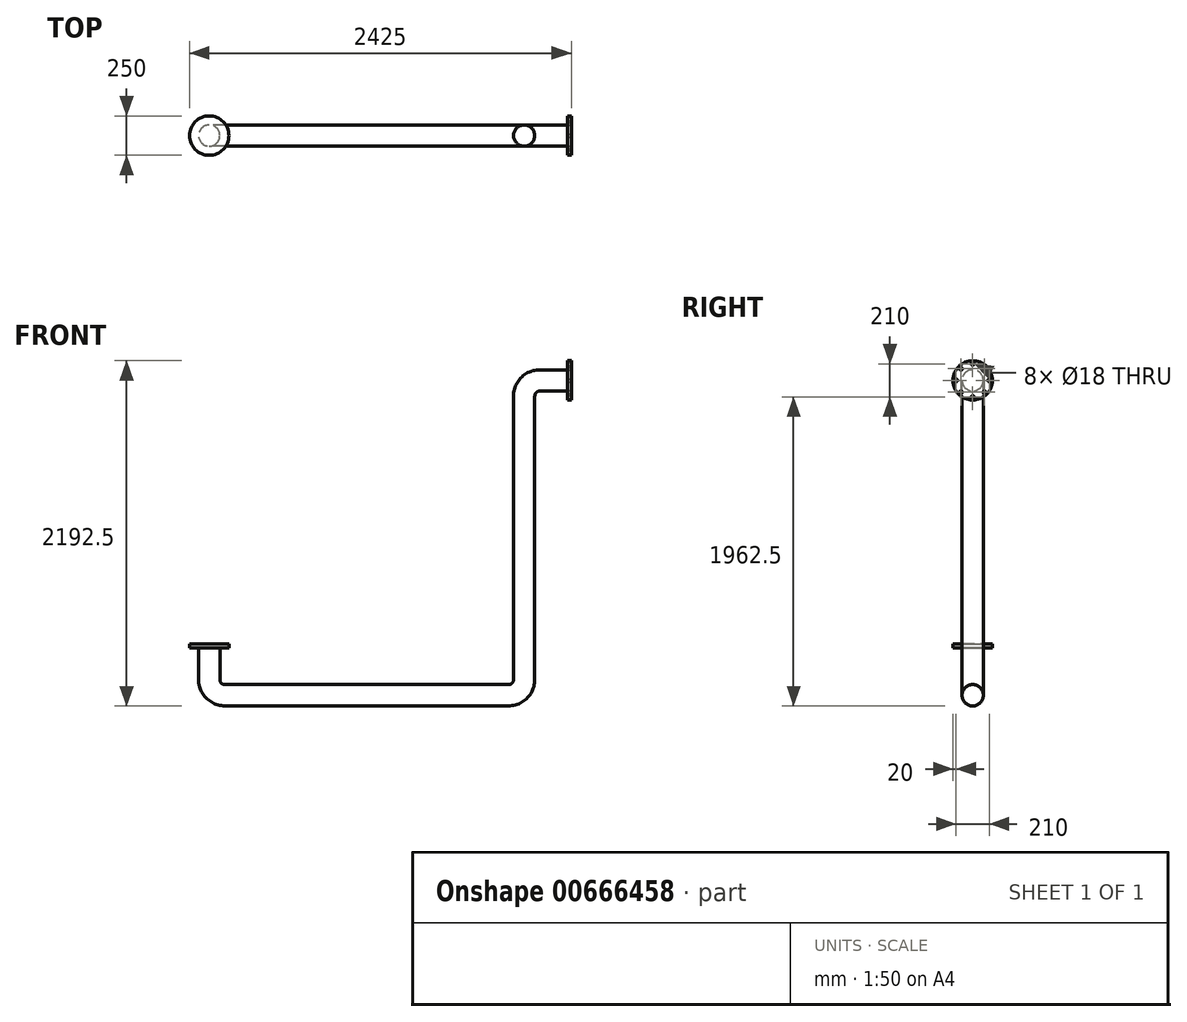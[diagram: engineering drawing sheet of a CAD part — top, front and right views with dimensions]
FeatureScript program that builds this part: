
annotation { "Feature Type Name" : "Feature", "Feature Type Description" : "" }
export const myFeature = defineFeature(function(context is Context, id is Id, definition is map)
    precondition{}
    {
        {
            var Q0;
            Q0=qCreatedBy(makeId("Front.planeOp"),FACE);
            var sketch = newSketch(context, id + "F0", { "sketchPlane" : qUnion([Q0])});
            skLineSegment(sketch, "E0", {"start": v(0, 0) * mm, "end": v(0, -200) * mm});
            skLineSegment(sketch, "E1", {"start": v(100, -300) * mm, "end": v(1900, -300) * mm});
            skLineSegment(sketch, "E2", {"start": v(2000, -200) * mm, "end": v(2000, 1600) * mm});
            skLineSegment(sketch, "E3", {"start": v(2100, 1700) * mm, "end": v(2300, 1700) * mm});
            skPoint(sketch, "E4.visualSharp", {"position": v(0, -300) * mm});
            skArc(sketch, "E4.filletArc", {"start": v(0, -200) * mm, "mid": v(29.29, -270.71) * mm, "end": v(100, -300) * mm});
            skPoint(sketch, "E5.visualSharp", {"position": v(2000, -300) * mm});
            skArc(sketch, "E5.filletArc", {"start": v(1900, -300) * mm, "mid": v(1970.71, -270.71) * mm, "end": v(2000, -200) * mm});
            skPoint(sketch, "E6.visualSharp", {"position": v(2000, 1700) * mm});
            skArc(sketch, "E6.filletArc", {"start": v(2100, 1700) * mm, "mid": v(2029.29, 1670.71) * mm, "end": v(2000, 1600) * mm});
            skSolve(sketch);
        }
        {
            var Q0;
            Q0=qCreatedBy(makeId("Top.planeOp"),FACE);
            var sketch = newSketch(context, id + "F1", { "sketchPlane" : qUnion([Q0])});
            skCircle(sketch, "E7", {"center": v(0, 0) * mm, "radius": 67.5 * mm});
            skCircle(sketch, "E8", {"center": v(0, 0) * mm, "radius": 125 * mm});
            skSolve(sketch);
        }
        {
            var Q0;
            Q0=makeQuery(id+"F1.imprint","IMPRINT",FACE,{"disambiguationData":[TD([[makeQuery(id+"F1.imprint","IMPRINT",EDGE,{"derivedFrom":sQuery(id+"F1.wireOp",EDGE,"E7")}),1.0]])]});
            var Q1;
            Q1=sQuery(id+"F0.wireOp",EDGE,"E0");
            var Q2;
            Q2=sQuery(id+"F0.wireOp",EDGE,"E4.filletArc");
            var Q3;
            Q3=sQuery(id+"F0.wireOp",EDGE,"E1");
            var Q4;
            Q4=sQuery(id+"F0.wireOp",EDGE,"E5.filletArc");
            var Q5;
            Q5=sQuery(id+"F0.wireOp",EDGE,"E2");
            var Q6;
            Q6=sQuery(id+"F0.wireOp",EDGE,"E6.filletArc");
            var Q7;
            Q7=sQuery(id+"F0.wireOp",EDGE,"E3");
            sweep(context, id + "F2", {"profiles" : qUnion([Q0]), "path" : qUnion([Q1, Q2, Q3, Q4, Q5, Q6, Q7])});
        }
        {
            var Q0;
            Q0 = qSketchRegion(id + "F1", true);
            var Q1;
            Q1=makeQuery(id+"F2.opSweep","CAP_FACE",FACE,{"disambiguationData":[OSD([sQuery(id+"F0.wireOp",VERTEX,"E0.start"),sQuery(id+"F1.wireOp",EDGE,"E7")])],"isStart":true});
            extrude(context, id + "F3", {"entities" : qUnion([Q0, Q1]), "operationType" : NewBodyOperationType.ADD, "depth" : 25 * mm, "offsetDistance" : 25 * mm});
        }
        {
            var Q0;
            Q0=makeQuery(id+"F2.opSweep","CAP_FACE",FACE,{"disambiguationData":[OSD([sQuery(id+"F0.wireOp",VERTEX,"E3.end"),sQuery(id+"F1.wireOp",EDGE,"E7")])],"isStart":false});
            var sketch = newSketch(context, id + "F4", { "sketchPlane" : qUnion([Q0])});
            skCircle(sketch, "E9", {"center": v(0, 1700) * mm, "radius": 125 * mm});
            skCircle(sketch, "E10", {"center": v(0, 1805) * mm, "radius": 9 * mm});
            skCircle(sketch, "E11.1.0", {"center": v(-74.25, 1774.25) * mm, "radius": 9 * mm});
            skCircle(sketch, "E11.2.0", {"center": v(-105, 1700) * mm, "radius": 9 * mm});
            skCircle(sketch, "E11.3.0", {"center": v(-74.25, 1625.75) * mm, "radius": 9 * mm});
            skCircle(sketch, "E11.4.0", {"center": v(0, 1595) * mm, "radius": 9 * mm});
            skCircle(sketch, "E11.5.0", {"center": v(74.25, 1625.75) * mm, "radius": 9 * mm});
            skCircle(sketch, "E11.6.0", {"center": v(105, 1700) * mm, "radius": 9 * mm});
            skCircle(sketch, "E11.7.0", {"center": v(74.25, 1774.25) * mm, "radius": 9 * mm});
            skSolve(sketch);
        }
        {
            var Q0;
            Q0=makeQuery(id+"F4.imprint","IMPRINT",FACE,{"disambiguationData":[TD([[makeQuery(id+"F4.imprint","IMPRINT",EDGE,{"derivedFrom":sQuery(id+"F4.wireOp",EDGE,"E9")}),1.0]])]});
            extrude(context, id + "F5", {"entities" : qUnion([Q0]), "operationType" : NewBodyOperationType.ADD, "oppositeDirection" : true, "depth" : 25 * mm, "offsetDistance" : 25 * mm});
        }
    });
